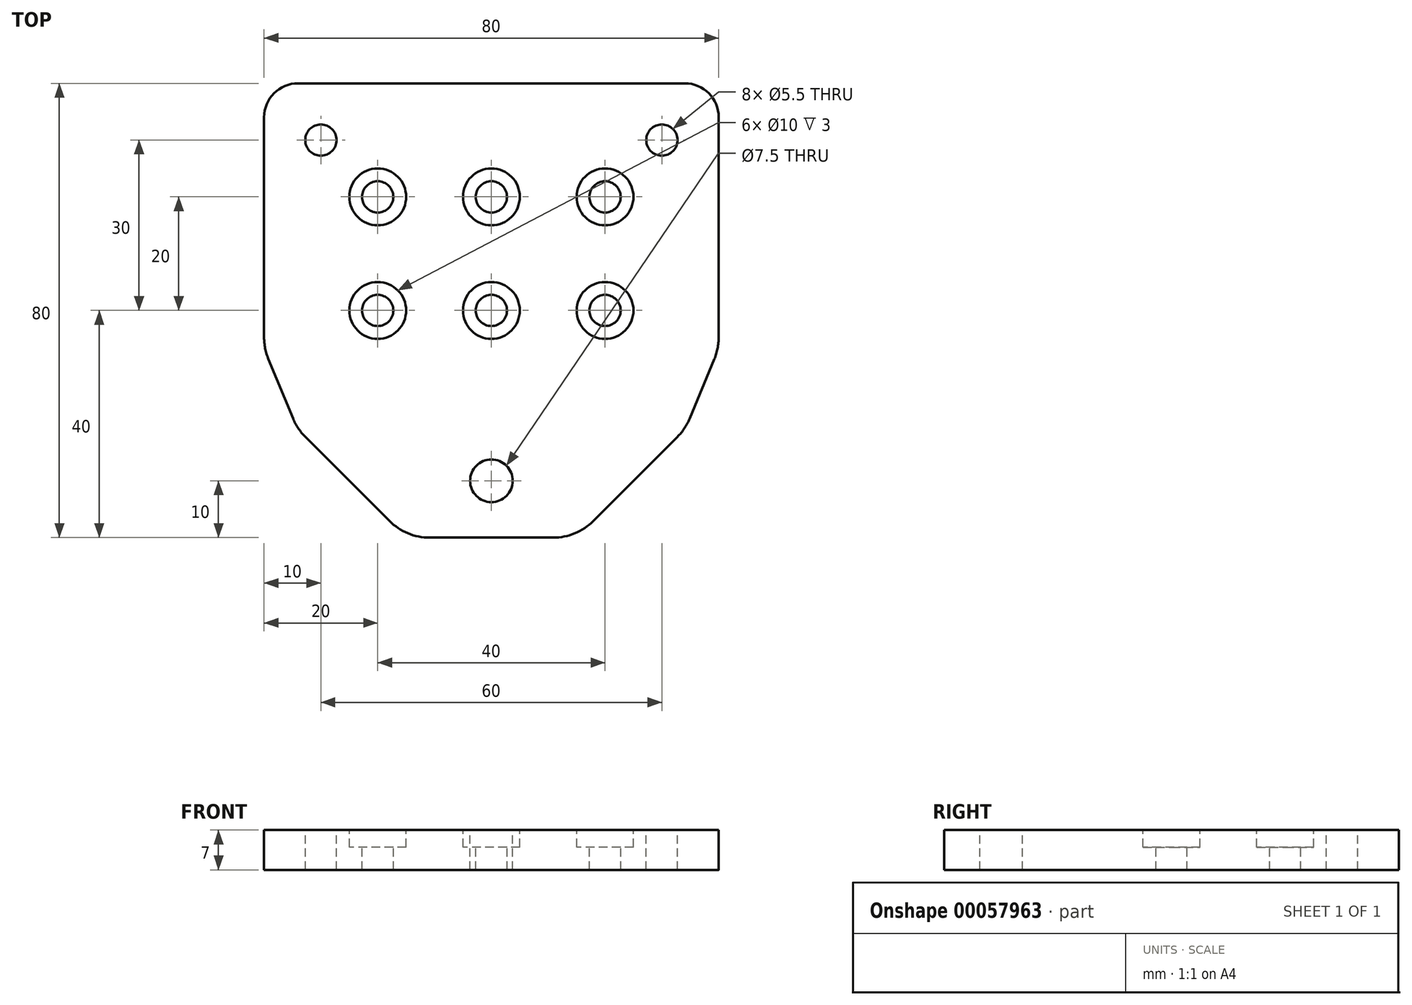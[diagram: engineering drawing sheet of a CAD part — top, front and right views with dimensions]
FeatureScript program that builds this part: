
annotation { "Feature Type Name" : "Feature", "Feature Type Description" : "" }
export const myFeature = defineFeature(function(context is Context, id is Id, definition is map)
    precondition{}
    {
        {
            var Q0;
            Q0=qCreatedBy(makeId("Top.planeOp"),FACE);
            var sketch = newSketch(context, id + "F0", { "sketchPlane" : qUnion([Q0])});
            skLineSegment(sketch, "E0.rect.bottom", {"start": v(40, 40) * mm, "end": v(-40, 40) * mm});
            skLineSegment(sketch, "E0.rect.top", {"start": v(40, -40) * mm, "end": v(-40, -40) * mm});
            skLineSegment(sketch, "E0.rect.left", {"start": v(40, 40) * mm, "end": v(40, -40) * mm});
            skLineSegment(sketch, "E0.rect.right", {"start": v(-40, 40) * mm, "end": v(-40, -40) * mm});
            skPoint(sketch, "E0.rect.middle", {"position": v(0, 0) * mm});
            skSolve(sketch);
        }
        {
            var Q0;
            Q0=makeQuery(id+"F0.imprint","IMPRINT",FACE,{"disambiguationData":[TD([[makeQuery(id+"F0.imprint","IMPRINT",EDGE,{"derivedFrom":sQuery(id+"F0.wireOp",EDGE,"E0.rect.bottom")}),1.0]])]});
            extrude(context, id + "F1", {"entities" : qUnion([Q0]), "depth" : 7 * mm});
        }
        {
            var Q0;
            Q0=makeQuery(id+"F1.opExtrude","CAP_FACE",FACE,{"disambiguationData":[OSD([sQuery(id+"F0.wireOp",EDGE,"E0.rect.bottom"),sQuery(id+"F0.wireOp",EDGE,"E0.rect.top"),sQuery(id+"F0.wireOp",EDGE,"E0.rect.left"),sQuery(id+"F0.wireOp",EDGE,"E0.rect.right")])],"isStart":false});
            var sketch = newSketch(context, id + "F2", { "sketchPlane" : qUnion([Q0])});
            skPoint(sketch, "E1", {"position": v(-30, 30) * mm});
            skPoint(sketch, "E2", {"position": v(30, 30) * mm});
            skPoint(sketch, "E3", {"position": v(0, -30) * mm});
            skSolve(sketch);
        }
        {
            var Q0;
            Q0=sQuery(id+"F2.wireOp",VERTEX,"E3");
            var Q1;
            Q1=makeQuery(id+"F1.opExtrude","SWEPT_BODY",BODY,{"disambiguationData":[OSD([sQuery(id+"F0.wireOp",EDGE,"E0.rect.bottom"),sQuery(id+"F0.wireOp",EDGE,"E0.rect.top"),sQuery(id+"F0.wireOp",EDGE,"E0.rect.left"),sQuery(id+"F0.wireOp",EDGE,"E0.rect.right")])]});
            hole(context, id + "F3", {"style" : HoleStyle.SIMPLE, "holeDiameter" : 7.5 * mm, "endStyle" : HoleEndStyle.THROUGH, "locations" : qUnion([Q0]), "scope" : qUnion([Q1])});
        }
        {
            var Q0;
            Q0=makeQuery(id+"F1.opExtrude","SWEPT_EDGE",EDGE,{"disambiguationData":[OSD([sQuery(id+"F0.wireOp",EDGE,"E0.rect.bottom"),sQuery(id+"F0.wireOp",EDGE,"E0.rect.right")])]});
            var Q1;
            Q1=makeQuery(id+"F1.opExtrude","SWEPT_EDGE",EDGE,{"disambiguationData":[OSD([sQuery(id+"F0.wireOp",EDGE,"E0.rect.bottom"),sQuery(id+"F0.wireOp",EDGE,"E0.rect.left")])]});
            fillet(context, id + "F4", {"entities" : qUnion([Q0, Q1]), "radius" : 6 * mm, "tangentPropagation" : true, "allowEdgeOverflow" : false});
        }
        {
            var Q0;
            Q0=makeQuery(id+"F1.opExtrude","SWEPT_EDGE",EDGE,{"disambiguationData":[OSD([sQuery(id+"F0.wireOp",EDGE,"E0.rect.top"),sQuery(id+"F0.wireOp",EDGE,"E0.rect.right")])]});
            var Q1;
            Q1=makeQuery(id+"F1.opExtrude","SWEPT_EDGE",EDGE,{"disambiguationData":[OSD([sQuery(id+"F0.wireOp",EDGE,"E0.rect.top"),sQuery(id+"F0.wireOp",EDGE,"E0.rect.left")])]});
            chamfer(context, id + "F5", {"entities" : qUnion([Q0, Q1]), "width" : 25 * mm, "tangentPropagation" : true});
        }
        {
            var Q0;
            {var subQ0=sQuery(id+"F0.wireOp",EDGE,"E0.rect.left");Q0=makeQuery(id+"F5.opChamfer","BLEND_EDGE",EDGE,{"blendedFrom":[makeQuery(id+"F1.opExtrude","SWEPT_EDGE",EDGE,{"disambiguationData":[OSD([sQuery(id+"F0.wireOp",EDGE,"E0.rect.top"),subQ0])]}),makeQuery(id+"F1.opExtrude","SWEPT_FACE",FACE,{"disambiguationData":[OSD([subQ0])]})],"blendedInto":[makeQuery(id+"F1.opExtrude","SWEPT_FACE",FACE,{"disambiguationData":[OSD([subQ0])]})]});}
            var Q1;
            {var subQ0=sQuery(id+"F0.wireOp",EDGE,"E0.rect.right");Q1=makeQuery(id+"F5.opChamfer","BLEND_EDGE",EDGE,{"blendedFrom":[makeQuery(id+"F1.opExtrude","SWEPT_EDGE",EDGE,{"disambiguationData":[OSD([sQuery(id+"F0.wireOp",EDGE,"E0.rect.top"),subQ0])]}),makeQuery(id+"F1.opExtrude","SWEPT_FACE",FACE,{"disambiguationData":[OSD([subQ0])]})],"blendedInto":[makeQuery(id+"F1.opExtrude","SWEPT_FACE",FACE,{"disambiguationData":[OSD([subQ0])]})]});}
            chamfer(context, id + "F6", {"entities" : qUnion([Q0, Q1]), "width" : 20 * mm, "tangentPropagation" : true});
        }
        {
            var Q0;
            Q0=makeQuery(id+"F1.opExtrude","CAP_FACE",FACE,{"disambiguationData":[OSD([sQuery(id+"F0.wireOp",EDGE,"E0.rect.bottom"),sQuery(id+"F0.wireOp",EDGE,"E0.rect.top"),sQuery(id+"F0.wireOp",EDGE,"E0.rect.left"),sQuery(id+"F0.wireOp",EDGE,"E0.rect.right")])],"isStart":false});
            var sketch = newSketch(context, id + "F7", { "sketchPlane" : qUnion([Q0])});
            skPoint(sketch, "E4", {"position": v(-20, 20) * mm});
            skPoint(sketch, "E5.0.1.0", {"position": v(-20, 0) * mm});
            skPoint(sketch, "E5.1.0.0", {"position": v(0, 20) * mm});
            skPoint(sketch, "E5.1.1.0", {"position": v(0, 0) * mm});
            skPoint(sketch, "E5.2.0.0", {"position": v(20, 20) * mm});
            skPoint(sketch, "E5.2.1.0", {"position": v(20, 0) * mm});
            skLineSegment(sketch, "E5.direction1", {"start": v(-20, 20) * mm, "end": v(0, 20) * mm, "construction": true});
            skLineSegment(sketch, "E5.direction2", {"start": v(-20, 20) * mm, "end": v(-20, 0) * mm, "construction": true});
            skSolve(sketch);
        }
        {
            var Q0;
            Q0=sQuery(id+"F7.wireOp",VERTEX,"E4");
            var Q1;
            Q1=sQuery(id+"F7.wireOp",VERTEX,"E5.1.0.0");
            var Q2;
            Q2=sQuery(id+"F7.wireOp",VERTEX,"E5.2.0.0");
            var Q3;
            Q3=sQuery(id+"F7.wireOp",VERTEX,"E5.2.1.0");
            var Q4;
            Q4=sQuery(id+"F7.wireOp",VERTEX,"E5.1.1.0");
            var Q5;
            Q5=sQuery(id+"F7.wireOp",VERTEX,"E5.0.1.0");
            var Q6;
            Q6=makeQuery(id+"F1.opExtrude","SWEPT_BODY",BODY,{"disambiguationData":[OSD([sQuery(id+"F0.wireOp",EDGE,"E0.rect.bottom"),sQuery(id+"F0.wireOp",EDGE,"E0.rect.top"),sQuery(id+"F0.wireOp",EDGE,"E0.rect.left"),sQuery(id+"F0.wireOp",EDGE,"E0.rect.right")])]});
            hole(context, id + "F8", {"style" : HoleStyle.C_BORE, "holeDiameter" : 5.5 * mm, "cBoreDiameter" : 10 * mm, "cBoreDepth" : 3 * mm, "endStyle" : HoleEndStyle.THROUGH, "locations" : qUnion([Q0, Q1, Q2, Q3, Q4, Q5]), "scope" : qUnion([Q6])});
        }
        {
            var Q0;
            {var subQ0=sQuery(id+"F0.wireOp",EDGE,"E0.rect.left");var subQ1=makeQuery(id+"F1.opExtrude","SWEPT_FACE",FACE,{"disambiguationData":[OSD([subQ0])]});Q0=makeQuery(id+"F6.opChamfer","BLEND_EDGE",EDGE,{"blendedFrom":[makeQuery(id+"F5.opChamfer","BLEND_EDGE",EDGE,{"blendedFrom":[makeQuery(id+"F1.opExtrude","SWEPT_EDGE",EDGE,{"disambiguationData":[OSD([sQuery(id+"F0.wireOp",EDGE,"E0.rect.top"),subQ0])]}),subQ1],"blendedInto":[subQ1]}),subQ1],"blendedInto":[subQ1]});}
            var Q1;
            {var subQ0=sQuery(id+"F0.wireOp",EDGE,"E0.rect.left");var subQ1=sQuery(id+"F0.wireOp",EDGE,"E0.rect.top");Q1=makeQuery(id+"F6.opChamfer","BLEND_EDGE",EDGE,{"blendedFrom":[makeQuery(id+"F5.opChamfer","BLEND_EDGE",EDGE,{"blendedFrom":[makeQuery(id+"F1.opExtrude","SWEPT_EDGE",EDGE,{"disambiguationData":[OSD([subQ1,subQ0])]}),makeQuery(id+"F1.opExtrude","SWEPT_FACE",FACE,{"disambiguationData":[OSD([subQ0])]})],"blendedInto":[makeQuery(id+"F1.opExtrude","SWEPT_FACE",FACE,{"disambiguationData":[OSD([subQ0])]})]}),makeQuery(id+"F5.opChamfer","BLEND_FACE",FACE,{"disambiguationData":[OSD([subQ1,subQ0])]})],"blendedInto":[makeQuery(id+"F5.opChamfer","BLEND_FACE",FACE,{"disambiguationData":[OSD([subQ1,subQ0])]})]});}
            var Q2;
            {var subQ0=sQuery(id+"F0.wireOp",EDGE,"E0.rect.top");Q2=makeQuery(id+"F5.opChamfer","BLEND_EDGE",EDGE,{"blendedFrom":[makeQuery(id+"F1.opExtrude","SWEPT_EDGE",EDGE,{"disambiguationData":[OSD([subQ0,sQuery(id+"F0.wireOp",EDGE,"E0.rect.left")])]}),makeQuery(id+"F1.opExtrude","SWEPT_FACE",FACE,{"disambiguationData":[OSD([subQ0])]})],"blendedInto":[makeQuery(id+"F1.opExtrude","SWEPT_FACE",FACE,{"disambiguationData":[OSD([subQ0])]})]});}
            var Q3;
            {var subQ0=sQuery(id+"F0.wireOp",EDGE,"E0.rect.top");Q3=makeQuery(id+"F5.opChamfer","BLEND_EDGE",EDGE,{"blendedFrom":[makeQuery(id+"F1.opExtrude","SWEPT_EDGE",EDGE,{"disambiguationData":[OSD([subQ0,sQuery(id+"F0.wireOp",EDGE,"E0.rect.right")])]}),makeQuery(id+"F1.opExtrude","SWEPT_FACE",FACE,{"disambiguationData":[OSD([subQ0])]})],"blendedInto":[makeQuery(id+"F1.opExtrude","SWEPT_FACE",FACE,{"disambiguationData":[OSD([subQ0])]})]});}
            var Q4;
            {var subQ0=sQuery(id+"F0.wireOp",EDGE,"E0.rect.right");var subQ1=makeQuery(id+"F1.opExtrude","SWEPT_FACE",FACE,{"disambiguationData":[OSD([subQ0])]});Q4=makeQuery(id+"F6.opChamfer","BLEND_EDGE",EDGE,{"blendedFrom":[makeQuery(id+"F5.opChamfer","BLEND_EDGE",EDGE,{"blendedFrom":[makeQuery(id+"F1.opExtrude","SWEPT_EDGE",EDGE,{"disambiguationData":[OSD([sQuery(id+"F0.wireOp",EDGE,"E0.rect.top"),subQ0])]}),subQ1],"blendedInto":[subQ1]}),subQ1],"blendedInto":[subQ1]});}
            var Q5;
            {var subQ0=sQuery(id+"F0.wireOp",EDGE,"E0.rect.right");var subQ1=sQuery(id+"F0.wireOp",EDGE,"E0.rect.top");Q5=makeQuery(id+"F6.opChamfer","BLEND_EDGE",EDGE,{"blendedFrom":[makeQuery(id+"F5.opChamfer","BLEND_EDGE",EDGE,{"blendedFrom":[makeQuery(id+"F1.opExtrude","SWEPT_EDGE",EDGE,{"disambiguationData":[OSD([subQ1,subQ0])]}),makeQuery(id+"F1.opExtrude","SWEPT_FACE",FACE,{"disambiguationData":[OSD([subQ0])]})],"blendedInto":[makeQuery(id+"F1.opExtrude","SWEPT_FACE",FACE,{"disambiguationData":[OSD([subQ0])]})]}),makeQuery(id+"F5.opChamfer","BLEND_FACE",FACE,{"disambiguationData":[OSD([subQ1,subQ0])]})],"blendedInto":[makeQuery(id+"F5.opChamfer","BLEND_FACE",FACE,{"disambiguationData":[OSD([subQ1,subQ0])]})]});}
            fillet(context, id + "F9", {"entities" : qUnion([Q0, Q1, Q2, Q3, Q4, Q5]), "radius" : 10 * mm, "tangentPropagation" : true, "allowEdgeOverflow" : false});
        }
        {
            var Q0;
            Q0=sQuery(id+"F2.wireOp",VERTEX,"E1");
            var Q1;
            Q1=sQuery(id+"F2.wireOp",VERTEX,"E2");
            var Q2;
            Q2=makeQuery(id+"F1.opExtrude","SWEPT_BODY",BODY,{"disambiguationData":[OSD([sQuery(id+"F0.wireOp",EDGE,"E0.rect.bottom"),sQuery(id+"F0.wireOp",EDGE,"E0.rect.top"),sQuery(id+"F0.wireOp",EDGE,"E0.rect.left"),sQuery(id+"F0.wireOp",EDGE,"E0.rect.right")])]});
            hole(context, id + "F10", {"style" : HoleStyle.SIMPLE, "holeDiameter" : 5.5 * mm, "endStyle" : HoleEndStyle.THROUGH, "locations" : qUnion([Q0, Q1]), "scope" : qUnion([Q2])});
        }
    });
